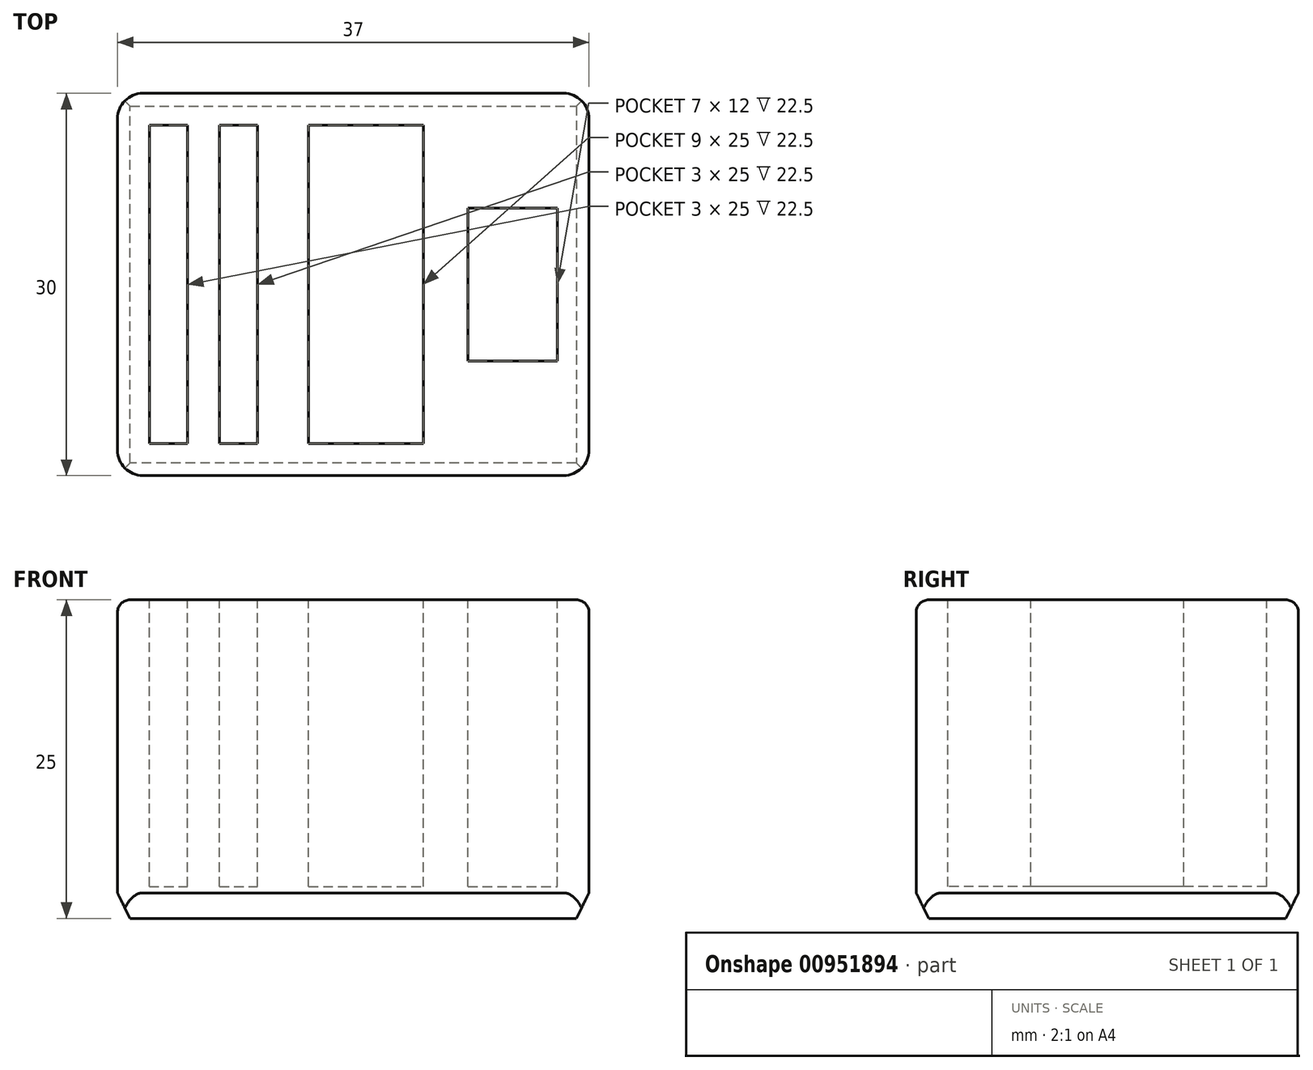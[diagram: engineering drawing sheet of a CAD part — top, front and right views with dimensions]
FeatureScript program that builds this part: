
annotation { "Feature Type Name" : "Feature", "Feature Type Description" : "" }
export const myFeature = defineFeature(function(context is Context, id is Id, definition is map)
    precondition{}
    {
        {
            var Q0;
            Q0=qCreatedBy(makeId("Top.planeOp"),FACE);
            var sketch = newSketch(context, id + "F0", { "sketchPlane" : qUnion([Q0])});
            skLineSegment(sketch, "E0.bottom", {"start": v(-21.53, 13.71) * mm, "end": v(15.47, 13.71) * mm});
            skLineSegment(sketch, "E0.top", {"start": v(-21.53, -16.29) * mm, "end": v(15.47, -16.29) * mm});
            skLineSegment(sketch, "E0.left", {"start": v(-21.53, 13.71) * mm, "end": v(-21.53, -16.29) * mm});
            skLineSegment(sketch, "E0.right", {"start": v(15.47, 13.71) * mm, "end": v(15.47, -16.29) * mm});
            skLineSegment(sketch, "E1.bottom", {"start": v(-19.03, 11.21) * mm, "end": v(-16.03, 11.21) * mm});
            skLineSegment(sketch, "E1.top", {"start": v(-19.03, -13.79) * mm, "end": v(-16.03, -13.79) * mm});
            skLineSegment(sketch, "E1.left", {"start": v(-19.03, 11.21) * mm, "end": v(-19.03, -13.79) * mm});
            skLineSegment(sketch, "E1.right", {"start": v(-16.03, 11.21) * mm, "end": v(-16.03, -13.79) * mm});
            skLineSegment(sketch, "E2.bottom", {"start": v(-13.53, 11.21) * mm, "end": v(-10.53, 11.21) * mm});
            skLineSegment(sketch, "E2.top", {"start": v(-13.53, -13.79) * mm, "end": v(-10.53, -13.79) * mm});
            skLineSegment(sketch, "E2.left", {"start": v(-13.53, 11.21) * mm, "end": v(-13.53, -13.79) * mm});
            skLineSegment(sketch, "E2.right", {"start": v(-10.53, 11.21) * mm, "end": v(-10.53, -13.79) * mm});
            skLineSegment(sketch, "E3.bottom", {"start": v(-6.53, 11.21) * mm, "end": v(2.47, 11.21) * mm});
            skLineSegment(sketch, "E3.top", {"start": v(-6.53, -13.79) * mm, "end": v(2.47, -13.79) * mm});
            skLineSegment(sketch, "E3.left", {"start": v(-6.53, 11.21) * mm, "end": v(-6.53, -13.79) * mm});
            skLineSegment(sketch, "E3.right", {"start": v(2.47, 11.21) * mm, "end": v(2.47, -13.79) * mm});
            skLineSegment(sketch, "E4.bottom", {"start": v(5.97, 4.71) * mm, "end": v(12.97, 4.71) * mm});
            skLineSegment(sketch, "E4.top", {"start": v(5.97, -7.29) * mm, "end": v(12.97, -7.29) * mm});
            skLineSegment(sketch, "E4.left", {"start": v(5.97, 4.71) * mm, "end": v(5.97, -7.29) * mm});
            skLineSegment(sketch, "E4.right", {"start": v(12.97, 4.71) * mm, "end": v(12.97, -7.29) * mm});
            skSolve(sketch);
        }
        {
            var Q0;
            Q0=makeQuery(id+"F0.imprint","IMPRINT",FACE,{"disambiguationData":[TD([[makeQuery(id+"F0.imprint","IMPRINT",EDGE,{"derivedFrom":sQuery(id+"F0.wireOp",EDGE,"E0.bottom")}),-1.0]])]});
            var Q1;
            Q1=makeQuery(id+"F0.imprint","IMPRINT",FACE,{"disambiguationData":[TD([[makeQuery(id+"F0.imprint","IMPRINT",EDGE,{"derivedFrom":sQuery(id+"F0.wireOp",EDGE,"E1.bottom")}),-1.0]])]});
            var Q2;
            Q2=makeQuery(id+"F0.imprint","IMPRINT",FACE,{"disambiguationData":[TD([[makeQuery(id+"F0.imprint","IMPRINT",EDGE,{"derivedFrom":sQuery(id+"F0.wireOp",EDGE,"E2.bottom")}),-1.0]])]});
            var Q3;
            Q3=makeQuery(id+"F0.imprint","IMPRINT",FACE,{"disambiguationData":[TD([[makeQuery(id+"F0.imprint","IMPRINT",EDGE,{"derivedFrom":sQuery(id+"F0.wireOp",EDGE,"E3.bottom")}),-1.0]])]});
            var Q4;
            Q4=makeQuery(id+"F0.imprint","IMPRINT",FACE,{"disambiguationData":[TD([[makeQuery(id+"F0.imprint","IMPRINT",EDGE,{"derivedFrom":sQuery(id+"F0.wireOp",EDGE,"E4.bottom")}),-1.0]])]});
            extrude(context, id + "F1", {"entities" : qUnion([Q0, Q1, Q2, Q3, Q4]), "oppositeDirection" : true, "depth" : 25 * mm, "offsetDistance" : 25 * mm});
        }
        {
            var Q0;
            Q0=makeQuery(id+"F0.imprint","IMPRINT",FACE,{"disambiguationData":[TD([[makeQuery(id+"F0.imprint","IMPRINT",EDGE,{"derivedFrom":sQuery(id+"F0.wireOp",EDGE,"E1.bottom")}),-1.0]])]});
            var Q1;
            Q1=makeQuery(id+"F0.imprint","IMPRINT",FACE,{"disambiguationData":[TD([[makeQuery(id+"F0.imprint","IMPRINT",EDGE,{"derivedFrom":sQuery(id+"F0.wireOp",EDGE,"E2.bottom")}),-1.0]])]});
            var Q2;
            Q2=makeQuery(id+"F0.imprint","IMPRINT",FACE,{"disambiguationData":[TD([[makeQuery(id+"F0.imprint","IMPRINT",EDGE,{"derivedFrom":sQuery(id+"F0.wireOp",EDGE,"E3.bottom")}),-1.0]])]});
            var Q3;
            Q3=makeQuery(id+"F0.imprint","IMPRINT",FACE,{"disambiguationData":[TD([[makeQuery(id+"F0.imprint","IMPRINT",EDGE,{"derivedFrom":sQuery(id+"F0.wireOp",EDGE,"E4.bottom")}),-1.0]])]});
            extrude(context, id + "F2", {"entities" : qUnion([Q0, Q1, Q2, Q3]), "operationType" : NewBodyOperationType.REMOVE, "oppositeDirection" : true, "depth" : 22.5 * mm, "offsetDistance" : 25 * mm});
        }
        {
            var Q0;
            Q0=makeQuery(id+"F1.opExtrude","CAP_EDGE",EDGE,{"disambiguationData":[OSD([sQuery(id+"F0.wireOp",EDGE,"E0.top")])],"isStart":false});
            var Q1;
            Q1=makeQuery(id+"F1.opExtrude","CAP_EDGE",EDGE,{"disambiguationData":[OSD([sQuery(id+"F0.wireOp",EDGE,"E0.right")])],"isStart":false});
            var Q2;
            Q2=makeQuery(id+"F1.opExtrude","CAP_EDGE",EDGE,{"disambiguationData":[OSD([sQuery(id+"F0.wireOp",EDGE,"E0.bottom")])],"isStart":false});
            var Q3;
            Q3=makeQuery(id+"F1.opExtrude","CAP_EDGE",EDGE,{"disambiguationData":[OSD([sQuery(id+"F0.wireOp",EDGE,"E0.left")])],"isStart":false});
            chamfer(context, id + "F3", {"entities" : qUnion([Q0, Q1, Q2, Q3]), "chamferType" : ChamferType.TWO_OFFSETS, "width1" : 2 * mm, "oppositeDirection" : false, "width2" : 1 * mm, "tangentPropagation" : true});
        }
        {
            var Q0;
            Q0=makeQuery(id+"F1.opExtrude","SWEPT_EDGE",EDGE,{"disambiguationData":[OSD([sQuery(id+"F0.wireOp",EDGE,"E0.top"),sQuery(id+"F0.wireOp",EDGE,"E0.left")])]});
            var Q1;
            Q1=makeQuery(id+"F1.opExtrude","SWEPT_EDGE",EDGE,{"disambiguationData":[OSD([sQuery(id+"F0.wireOp",EDGE,"E0.bottom"),sQuery(id+"F0.wireOp",EDGE,"E0.left")])]});
            var Q2;
            Q2=makeQuery(id+"F1.opExtrude","SWEPT_EDGE",EDGE,{"disambiguationData":[OSD([sQuery(id+"F0.wireOp",EDGE,"E0.bottom"),sQuery(id+"F0.wireOp",EDGE,"E0.right")])]});
            var Q3;
            Q3=makeQuery(id+"F1.opExtrude","SWEPT_EDGE",EDGE,{"disambiguationData":[OSD([sQuery(id+"F0.wireOp",EDGE,"E0.top"),sQuery(id+"F0.wireOp",EDGE,"E0.right")])]});
            fillet(context, id + "F4", {"entities" : qUnion([Q0, Q1, Q2, Q3]), "radius" : 2 * mm, "tangentPropagation" : true, "allowEdgeOverflow" : false});
        }
        {
            var Q0;
            Q0=makeQuery(id+"F2.boolean.opBoolean","COPY",EDGE,{"derivedFrom":makeQuery(id+"F2.opExtrude","CAP_EDGE",EDGE,{"disambiguationData":[OSD([sQuery(id+"F0.wireOp",EDGE,"E4.right")])],"isStart":true})});
            var Q1;
            Q1=makeQuery(id+"F2.boolean.opBoolean","COPY",EDGE,{"derivedFrom":makeQuery(id+"F2.opExtrude","CAP_EDGE",EDGE,{"disambiguationData":[OSD([sQuery(id+"F0.wireOp",EDGE,"E4.top")])],"isStart":true})});
            var Q2;
            Q2=makeQuery(id+"F2.boolean.opBoolean","COPY",EDGE,{"derivedFrom":makeQuery(id+"F2.opExtrude","CAP_EDGE",EDGE,{"disambiguationData":[OSD([sQuery(id+"F0.wireOp",EDGE,"E4.left")])],"isStart":true})});
            var Q3;
            Q3=makeQuery(id+"F2.boolean.opBoolean","COPY",EDGE,{"derivedFrom":makeQuery(id+"F2.opExtrude","CAP_EDGE",EDGE,{"disambiguationData":[OSD([sQuery(id+"F0.wireOp",EDGE,"E4.bottom")])],"isStart":true})});
            var Q4;
            Q4=makeQuery(id+"F2.boolean.opBoolean","COPY",EDGE,{"derivedFrom":makeQuery(id+"F2.opExtrude","CAP_EDGE",EDGE,{"disambiguationData":[OSD([sQuery(id+"F0.wireOp",EDGE,"E3.right")])],"isStart":true})});
            var Q5;
            Q5=makeQuery(id+"F2.boolean.opBoolean","COPY",EDGE,{"derivedFrom":makeQuery(id+"F2.opExtrude","CAP_EDGE",EDGE,{"disambiguationData":[OSD([sQuery(id+"F0.wireOp",EDGE,"E3.top")])],"isStart":true})});
            var Q6;
            Q6=makeQuery(id+"F2.boolean.opBoolean","COPY",EDGE,{"derivedFrom":makeQuery(id+"F2.opExtrude","CAP_EDGE",EDGE,{"disambiguationData":[OSD([sQuery(id+"F0.wireOp",EDGE,"E3.left")])],"isStart":true})});
            var Q7;
            Q7=makeQuery(id+"F2.boolean.opBoolean","COPY",EDGE,{"derivedFrom":makeQuery(id+"F2.opExtrude","CAP_EDGE",EDGE,{"disambiguationData":[OSD([sQuery(id+"F0.wireOp",EDGE,"E3.bottom")])],"isStart":true})});
            var Q8;
            Q8=makeQuery(id+"F2.boolean.opBoolean","COPY",EDGE,{"derivedFrom":makeQuery(id+"F2.opExtrude","CAP_EDGE",EDGE,{"disambiguationData":[OSD([sQuery(id+"F0.wireOp",EDGE,"E2.right")])],"isStart":true})});
            var Q9;
            Q9=makeQuery(id+"F2.boolean.opBoolean","COPY",EDGE,{"derivedFrom":makeQuery(id+"F2.opExtrude","CAP_EDGE",EDGE,{"disambiguationData":[OSD([sQuery(id+"F0.wireOp",EDGE,"E2.top")])],"isStart":true})});
            var Q10;
            Q10=makeQuery(id+"F2.boolean.opBoolean","COPY",EDGE,{"derivedFrom":makeQuery(id+"F2.opExtrude","CAP_EDGE",EDGE,{"disambiguationData":[OSD([sQuery(id+"F0.wireOp",EDGE,"E2.left")])],"isStart":true})});
            var Q11;
            Q11=makeQuery(id+"F2.boolean.opBoolean","COPY",EDGE,{"derivedFrom":makeQuery(id+"F2.opExtrude","CAP_EDGE",EDGE,{"disambiguationData":[OSD([sQuery(id+"F0.wireOp",EDGE,"E2.bottom")])],"isStart":true})});
            var Q12;
            Q12=makeQuery(id+"F2.boolean.opBoolean","COPY",EDGE,{"derivedFrom":makeQuery(id+"F2.opExtrude","CAP_EDGE",EDGE,{"disambiguationData":[OSD([sQuery(id+"F0.wireOp",EDGE,"E1.right")])],"isStart":true})});
            var Q13;
            Q13=makeQuery(id+"F2.boolean.opBoolean","COPY",EDGE,{"derivedFrom":makeQuery(id+"F2.opExtrude","CAP_EDGE",EDGE,{"disambiguationData":[OSD([sQuery(id+"F0.wireOp",EDGE,"E1.bottom")])],"isStart":true})});
            var Q14;
            Q14=makeQuery(id+"F2.boolean.opBoolean","COPY",EDGE,{"derivedFrom":makeQuery(id+"F2.opExtrude","CAP_EDGE",EDGE,{"disambiguationData":[OSD([sQuery(id+"F0.wireOp",EDGE,"E1.left")])],"isStart":true})});
            var Q15;
            Q15=makeQuery(id+"F2.boolean.opBoolean","COPY",EDGE,{"derivedFrom":makeQuery(id+"F2.opExtrude","CAP_EDGE",EDGE,{"disambiguationData":[OSD([sQuery(id+"F0.wireOp",EDGE,"E1.top")])],"isStart":true})});
            var Q16;
            Q16=makeQuery(id+"F1.opExtrude","CAP_EDGE",EDGE,{"disambiguationData":[OSD([sQuery(id+"F0.wireOp",EDGE,"E0.bottom")])],"isStart":true});
            fillet(context, id + "F5", {"entities" : qUnion([Q0, Q1, Q2, Q3, Q4, Q5, Q6, Q7, Q8, Q9, Q10, Q11, Q12, Q13, Q14, Q15, Q16]), "radius" : 1 * mm, "tangentPropagation" : true, "allowEdgeOverflow" : false});
        }
    });
